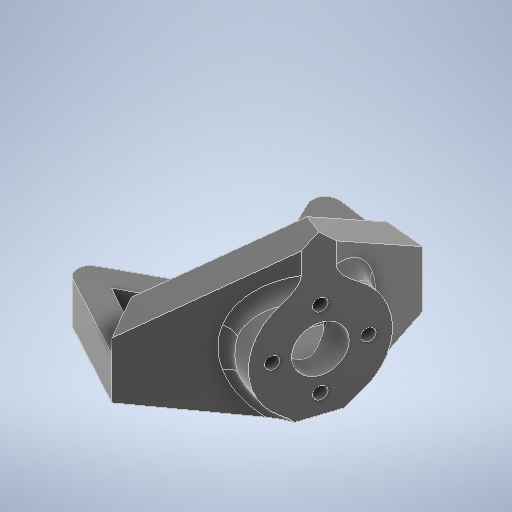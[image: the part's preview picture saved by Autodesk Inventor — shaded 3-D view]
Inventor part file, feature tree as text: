
AUTODESK INVENTOR PART (.ipt)
format: ipt  version: 2025.1 (Build 291241000, 241)  size: 643,072 bytes
history: native  units: mm
features: extrude x15, projected_geometry x13, sketch x12, fillet x4, chamfer x3, other x2
ambient origin geometry x8: Origin, YZ Plane, XZ Plane, XY Plane, X Axis, Y Axis, Z Axis, Center Point
bodies: Body1 (feature_tree)
feature tree (49):
  other  "ソリッド1"
  sketch  "スケッチ1"
  extrude  "押し出し1"  Depth=12.0mm
  extrude  "押し出し2"  Depth=15.0mm
  extrude  "押し出し3"  Depth=3.0mm
  extrude  "押し出し4"  Depth=3.141593mm
  extrude  "押し出し5"  Depth=2.0mm
  chamfer  "面取り1"  Distance=40.0mm
  chamfer  "面取り2"  Distance=13.0mm
  extrude  "押し出し6"  Depth=3.0mm
  chamfer  "面取り4"  Distance=3.0mm
  extrude  "押し出し8"  Depth=23.75mm TaperAngle=0.0deg
  extrude  "押し出し9"  Depth=1.0mm TaperAngle=0.0deg
  fillet  "フィレット3"  Radius=10.0mm
  extrude  "押し出し10"  Depth=38.0mm TaperAngle=0.0deg
  extrude  "押し出し11"  Depth=20.75mm TaperAngle=0.0deg
  fillet  "フィレット4"  Radius=2.0mm
  extrude  "押し出し12"  Depth=2.0mm TaperAngle=45.0deg
  fillet  "フィレット5"  Radius=13.75mm
  extrude  "押し出し13"  Depth=2.0mm TaperAngle=45.0deg
  fillet  "フィレット6"  Radius=5.25mm
  sketch  "スケッチ12"
  extrude  "押し出し14"  Depth=9.25mm TaperAngle=0.0deg
  extrude  "押し出し15"  Depth=3.25mm
  extrude  "押し出し16"  Depth=3.0mm
  sketch  "スケッチ2"
  projected_geometry  "投影ループ1"
  sketch  "スケッチ3"
  projected_geometry  "投影ループ2"
  projected_geometry  "投影ループ3"
  projected_geometry  "投影ループ4"
  projected_geometry  "投影ループ5"
  sketch  "スケッチ4"
  projected_geometry  "投影ループ6"
  sketch  "スケッチ6"
  sketch  "スケッチ7"
  projected_geometry  "投影ループ8"
  sketch  "スケッチ8"
  projected_geometry  "投影ループ9"
  sketch  "スケッチ9"
  projected_geometry  "投影ループ10"
  sketch  "スケッチ10"
  projected_geometry  "投影ループ11"
  sketch  "スケッチ11"
  other  "スケッチ円形状パターン1"
  sketch  "スケッチ13"
  projected_geometry  "投影ループ12"
  projected_geometry  "投影ループ13"
  projected_geometry  "投影ループ14"
